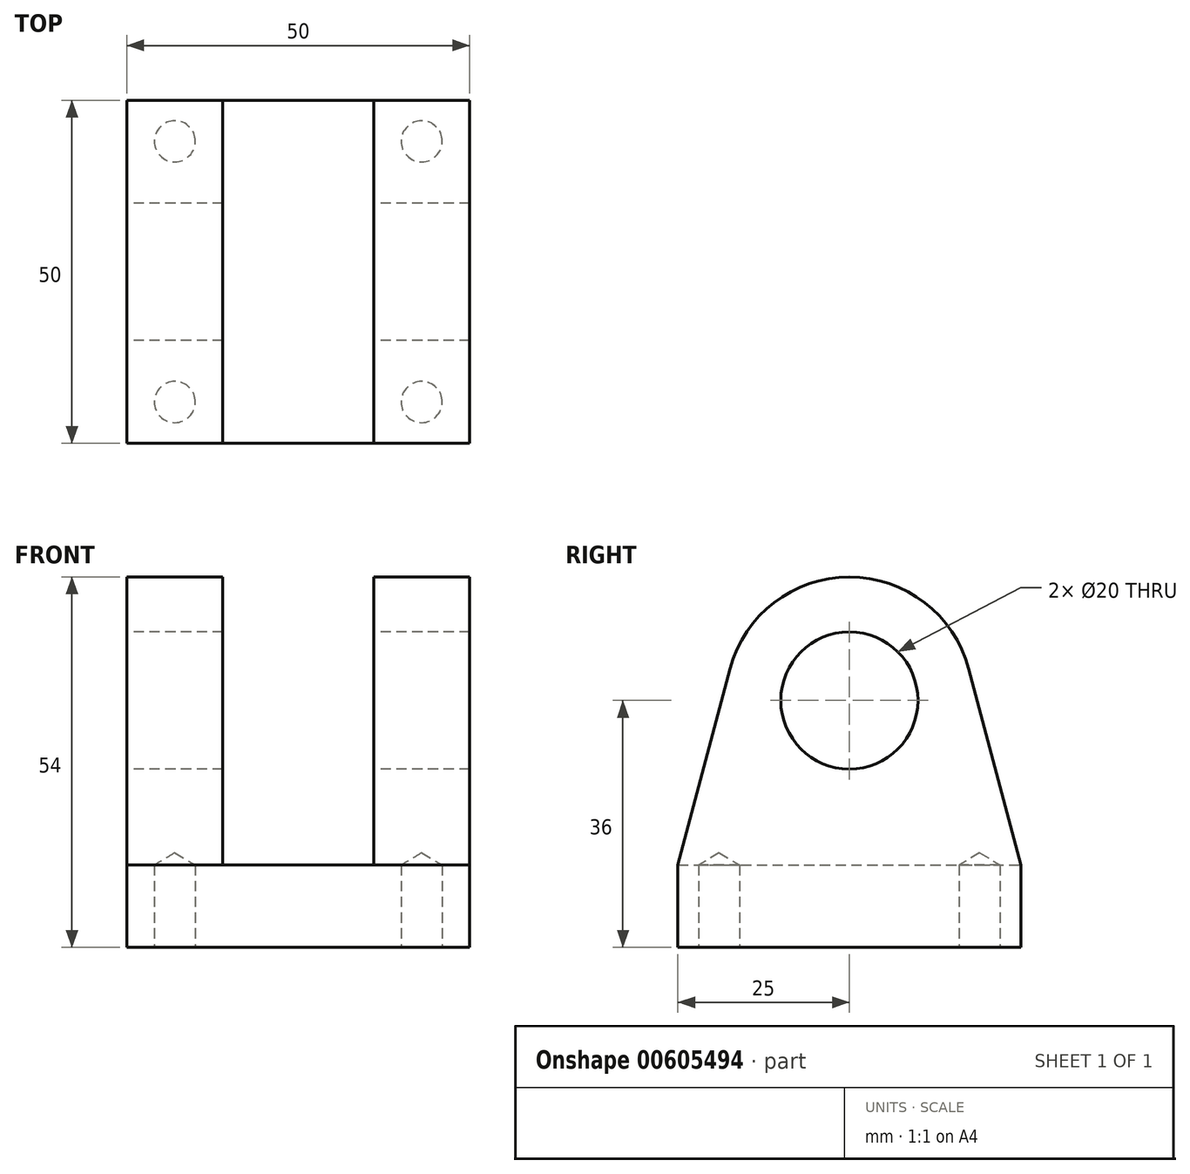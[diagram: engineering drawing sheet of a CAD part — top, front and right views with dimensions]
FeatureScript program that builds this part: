
annotation { "Feature Type Name" : "Feature", "Feature Type Description" : "" }
export const myFeature = defineFeature(function(context is Context, id is Id, definition is map)
    precondition{}
    {
        {
            var Q0;
            Q0=qCreatedBy(makeId("Right.planeOp"),FACE);
            var sketch = newSketch(context, id + "F0", { "sketchPlane" : qUnion([Q0])});
            skLineSegment(sketch, "E0", {"start": v(0, 0) * mm, "end": v(50, 0) * mm});
            skLineSegment(sketch, "E1", {"start": v(25, 0) * mm, "end": v(25, 36) * mm, "construction": true});
            skCircle(sketch, "E2", {"center": v(25, 36) * mm, "radius": 10 * mm});
            skArc(sketch, "E3", {"start": v(42.4, 40.62) * mm, "mid": v(25, 54) * mm, "end": v(7.6, 40.62) * mm});
            skLineSegment(sketch, "E4", {"start": v(0, 0) * mm, "end": v(0, 12) * mm});
            skLineSegment(sketch, "E5", {"start": v(0, 12) * mm, "end": v(7.6, 40.62) * mm});
            skLineSegment(sketch, "E6.MirrorCS", {"start": v(50, 0) * mm, "end": v(50, 12) * mm});
            skLineSegment(sketch, "E7.MirrorCS", {"start": v(50, 12) * mm, "end": v(42.4, 40.62) * mm});
            skSolve(sketch);
        }
        {
            var Q0;
            Q0 = qSketchRegion(id + "F0", true);
            extrude(context, id + "F1", {"entities" : qUnion([Q0]), "depth" : 50 * mm, "offsetDistance" : 25 * mm});
        }
        {
            var Q0;
            Q0=makeQuery(id+"F1.opExtrude","SWEPT_FACE",FACE,{"disambiguationData":[OSD([sQuery(id+"F0.wireOp",EDGE,"E6.MirrorCS")])]});
            var sketch = newSketch(context, id + "F2", { "sketchPlane" : qUnion([Q0])});
            skLineSegment(sketch, "E8.bottom", {"start": v(-36, 12) * mm, "end": v(-14, 12) * mm});
            skLineSegment(sketch, "E8.top", {"start": v(-36, 63.65) * mm, "end": v(-14, 63.65) * mm});
            skLineSegment(sketch, "E8.left", {"start": v(-36, 12) * mm, "end": v(-36, 63.65) * mm});
            skLineSegment(sketch, "E8.right", {"start": v(-14, 12) * mm, "end": v(-14, 63.65) * mm});
            skSolve(sketch);
        }
        {
            var Q0;
            Q0 = qSketchRegion(id + "F2", true);
            extrude(context, id + "F3", {"entities" : qUnion([Q0]), "operationType" : NewBodyOperationType.REMOVE, "oppositeDirection" : true, "depth" : 61.9 * mm, "offsetDistance" : 25 * mm});
        }
        {
            var Q0;
            Q0=makeQuery(id+"F1.opExtrude","SWEPT_FACE",FACE,{"disambiguationData":[OSD([sQuery(id+"F0.wireOp",EDGE,"E0")])]});
            var sketch = newSketch(context, id + "F4", { "sketchPlane" : qUnion([Q0])});
            skPoint(sketch, "E9", {"position": v(7, -6) * mm});
            skPoint(sketch, "E10", {"position": v(43, -6) * mm});
            skPoint(sketch, "E11", {"position": v(43, -44) * mm});
            skPoint(sketch, "E12", {"position": v(7, -44) * mm});
            skSolve(sketch);
        }
        {
            var Q0;
            Q0=sQuery(id+"F4.wireOp",VERTEX,"E9");
            var Q1;
            Q1=sQuery(id+"F4.wireOp",VERTEX,"E12");
            var Q2;
            Q2=sQuery(id+"F4.wireOp",VERTEX,"E11");
            var Q3;
            Q3=sQuery(id+"F4.wireOp",VERTEX,"E10");
            var Q4;
            Q4=makeQuery(id+"F1.opExtrude","SWEPT_BODY",BODY,{"disambiguationData":[OSD([sQuery(id+"F0.wireOp",EDGE,"E0"),sQuery(id+"F0.wireOp",EDGE,"E2"),sQuery(id+"F0.wireOp",EDGE,"E3"),sQuery(id+"F0.wireOp",EDGE,"E4"),sQuery(id+"F0.wireOp",EDGE,"E5"),sQuery(id+"F0.wireOp",EDGE,"E6.MirrorCS"),sQuery(id+"F0.wireOp",EDGE,"E7.MirrorCS")])]});
            hole(context, id + "F5", {"style" : HoleStyle.SIMPLE, "endStyle" : HoleEndStyle.BLIND, "holeDiameter" : 6 * mm, "majorDiameter" : 5 * mm, "holeDepth" : 12 * mm, "isTappedThrough" : true, "tappedDepth" : 12 * mm, "tapClearance" : 3, "locations" : qUnion([Q0, Q1, Q2, Q3]), "scope" : qUnion([Q4])});
        }
    });
